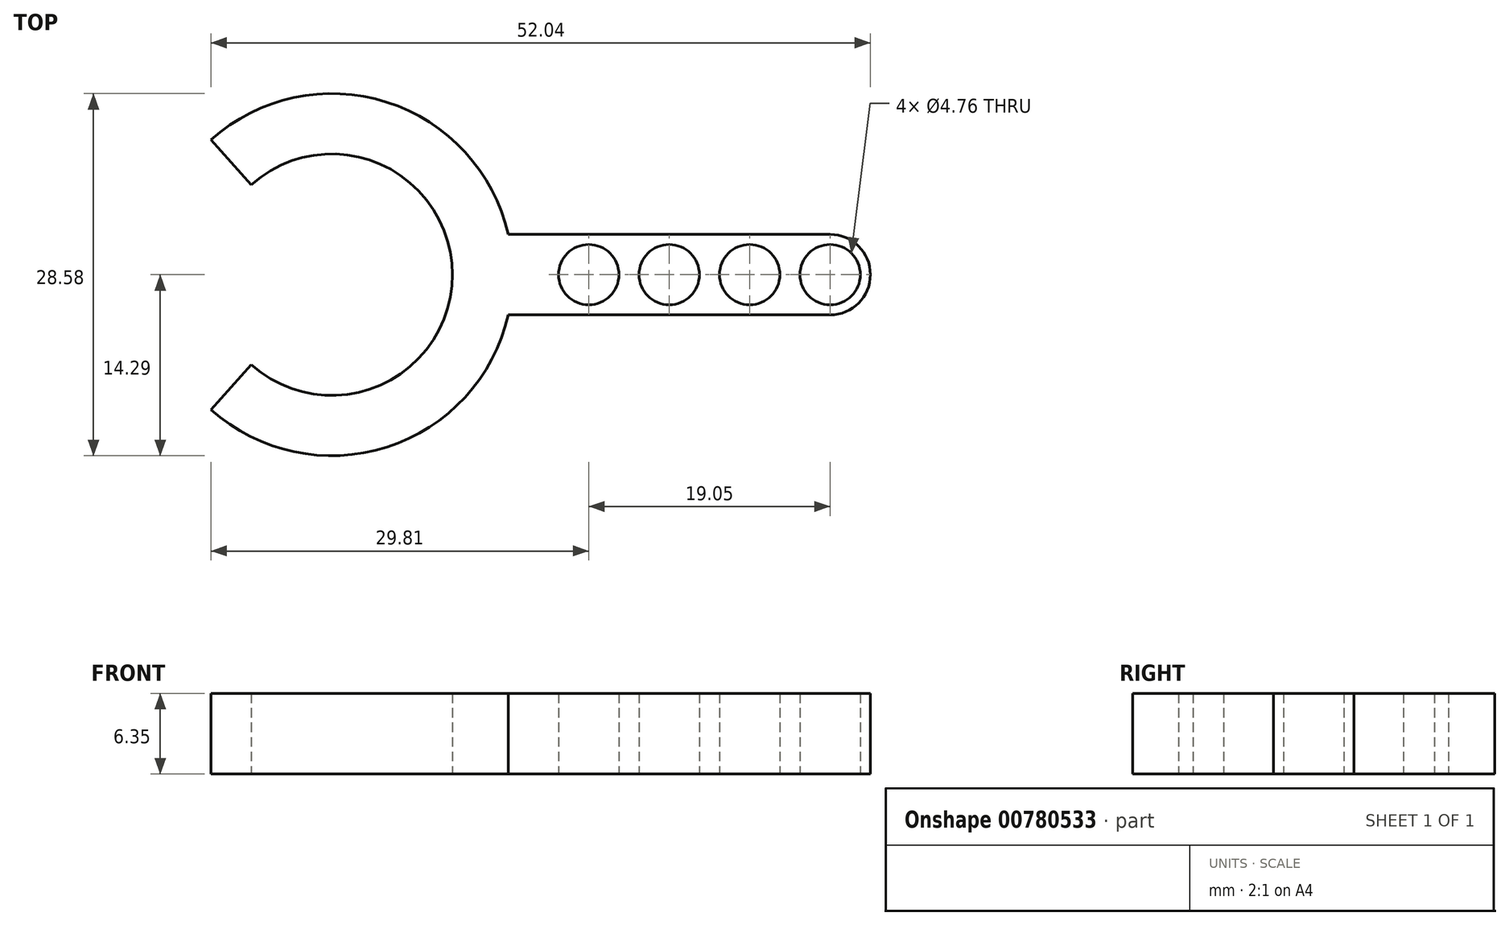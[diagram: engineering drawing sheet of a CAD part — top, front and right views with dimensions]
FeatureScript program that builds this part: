
annotation { "Feature Type Name" : "Feature", "Feature Type Description" : "" }
export const myFeature = defineFeature(function(context is Context, id is Id, definition is map)
    precondition{}
    {
        {
            var Q0;
            Q0=qCreatedBy(makeId("Top.planeOp"),FACE);
            var sketch = newSketch(context, id + "F0", { "sketchPlane" : qUnion([Q0])});
            skArc(sketch, "E0", {"start": v(-6.35, 7.1) * mm, "mid": v(9.53, 0) * mm, "end": v(-6.35, -7.1) * mm});
            skArc(sketch, "E1", {"start": v(-9.53, 10.65) * mm, "mid": v(14.29, 0) * mm, "end": v(-9.53, -10.65) * mm});
            skLineSegment(sketch, "E2", {"start": v(-9.53, -10.65) * mm, "end": v(-6.35, -7.1) * mm});
            skLineSegment(sketch, "E3", {"start": v(-9.52, 10.65) * mm, "end": v(-6.35, 7.1) * mm});
            skSolve(sketch);
        }
        {
            var Q0;
            Q0=qSketchRegion(id+"F0",true);
            extrude(context, id + "F1", {"entities" : qUnion([Q0]), "depth" : 6.35 * mm, "offsetDistance" : 25.4 * mm});
        }
        {
            var Q0;
            Q0=qCreatedBy(makeId("Top.planeOp"),FACE);
            var sketch = newSketch(context, id + "F2", { "sketchPlane" : qUnion([Q0])});
            skLineSegment(sketch, "E4", {"start": v(13.93, 3.18) * mm, "end": v(39.33, 3.18) * mm});
            skLineSegment(sketch, "E5", {"start": v(13.93, -3.17) * mm, "end": v(39.33, -3.17) * mm});
            skArc(sketch, "E6", {"start": v(39.33, 3.18) * mm, "mid": v(42.5, 0) * mm, "end": v(39.33, -3.18) * mm});
            skCircle(sketch, "E7", {"center": v(39.33, 0) * mm, "radius": 2.38 * mm});
            skArc(sketch, "E8", {"start": v(13.93, -3.18) * mm, "mid": v(14.29, 0) * mm, "end": v(13.93, 3.18) * mm});
            skCircle(sketch, "E9.1.0.0", {"center": v(32.98, 0) * mm, "radius": 2.38 * mm});
            skCircle(sketch, "E9.2.0.0", {"center": v(26.63, 0) * mm, "radius": 2.38 * mm});
            skCircle(sketch, "E9.3.0.0", {"center": v(20.28, 0) * mm, "radius": 2.38 * mm});
            skLineSegment(sketch, "E9.direction1", {"start": v(39.33, 0) * mm, "end": v(32.98, 0) * mm, "construction": true});
            skSolve(sketch);
        }
        {
            var Q0;
            Q0=qSketchRegion(id+"F2",true);
            var Q1;
            Q1=makeQuery(id+"F1.opExtrude","CAP_FACE",FACE,{"disambiguationData":[OSD([sQuery(id+"F0.wireOp",EDGE,"E0"),sQuery(id+"F0.wireOp",EDGE,"E1"),sQuery(id+"F0.wireOp",EDGE,"E2"),sQuery(id+"F0.wireOp",EDGE,"E3")])],"isStart":false});
            extrude(context, id + "F3", {"entities" : qUnion([Q0]), "operationType" : NewBodyOperationType.ADD, "endBound" : BoundingType.UP_TO_SURFACE, "depth" : 25.4 * mm, "endBoundEntityFace" : qUnion([Q1]), "offsetDistance" : 25.4 * mm});
        }
    });
